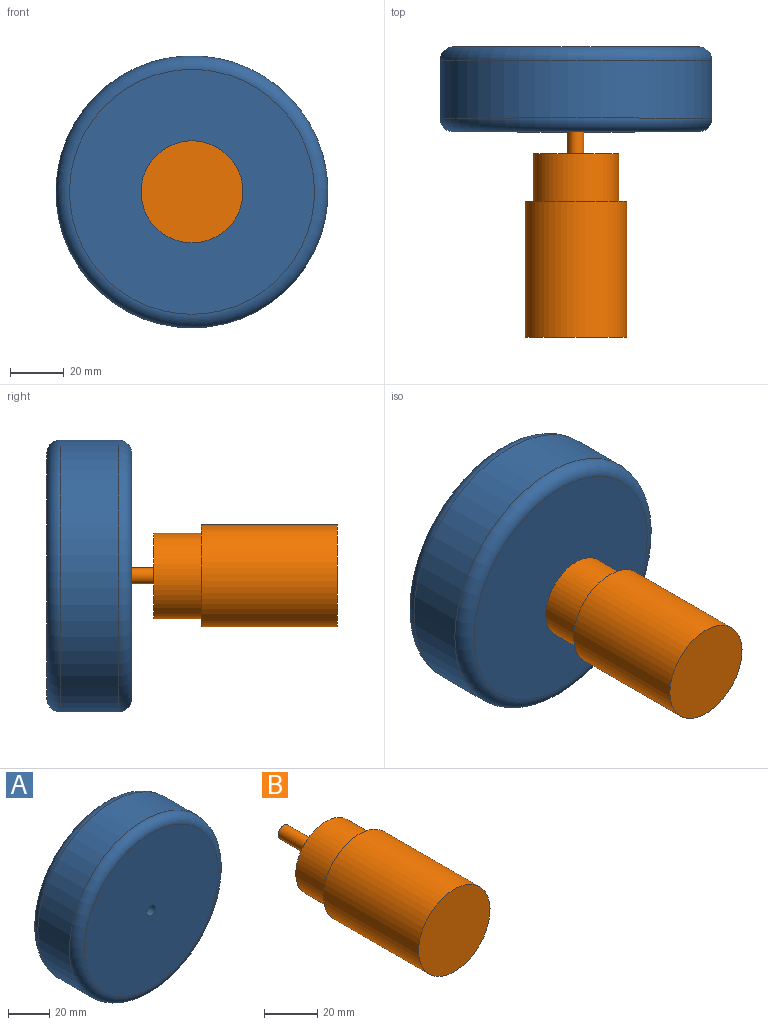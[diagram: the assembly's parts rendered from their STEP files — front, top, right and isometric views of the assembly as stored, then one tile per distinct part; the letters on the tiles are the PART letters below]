
ASSEMBLY  parts=2 mates=1
PART A: 6 faces, bbox 110x31.8x110 mm
  f0: cylinder r=3mm len=31.75mm, axis (0,1,0), area 598.5mm2, adj f2,f3
  f1: cylinder r=50.8mm len=101.6mm, axis (0,1,0), area 6891.2mm2, adj f4,f5
  f2: plane 91.44x91.44mm, normal (0,-1,0), area 6538.7mm2, adj f0,f5
  f3: plane 91.44x91.44mm, normal (0,1,0), area 6538.7mm2, adj f0,f4
  f4: torus R=45.72mm, axis (0,-1,0), area 2454.4mm2, adj f1,f3
  f5: torus R=45.72mm, axis (0,-1,0), area 2454.4mm2, adj f1,f2
PART B: 7 faces, bbox 38.1x91.1x38.1 mm
  f0: cylinder r=16mm len=32mm, axis (0,1,0), area 1787.4mm2, adj f1,f4
  f1: plane 32x32mm, normal (0,1,0), area 776mm2, adj f0,f5
  f2: cylinder r=19.05mm len=50.8mm, axis (0,1,0), area 6080.5mm2, adj f3,f4
  f3: plane 38.1x38.1mm, normal (0,-1,0), area 1140.1mm2, adj f2
  f4: plane 38.1x38.1mm, normal (0,1,0), area 335.8mm2, adj f0,f2
  f5: cylinder r=3mm len=22.48mm, axis (0,-1,0), area 423.7mm2, adj f1,f6
  f6: plane 6x6mm, normal (0,1,0), area 28.3mm2, adj f5
PLACE A t=(95.57,57.68,-0.15)mm
PLACE B t=(95.57,17.77,-0.15)mm
MATE cylindrical B.f5 <-> A.f0  axis (0,-1,0) through (95.57,40.24,-0.15)mm
